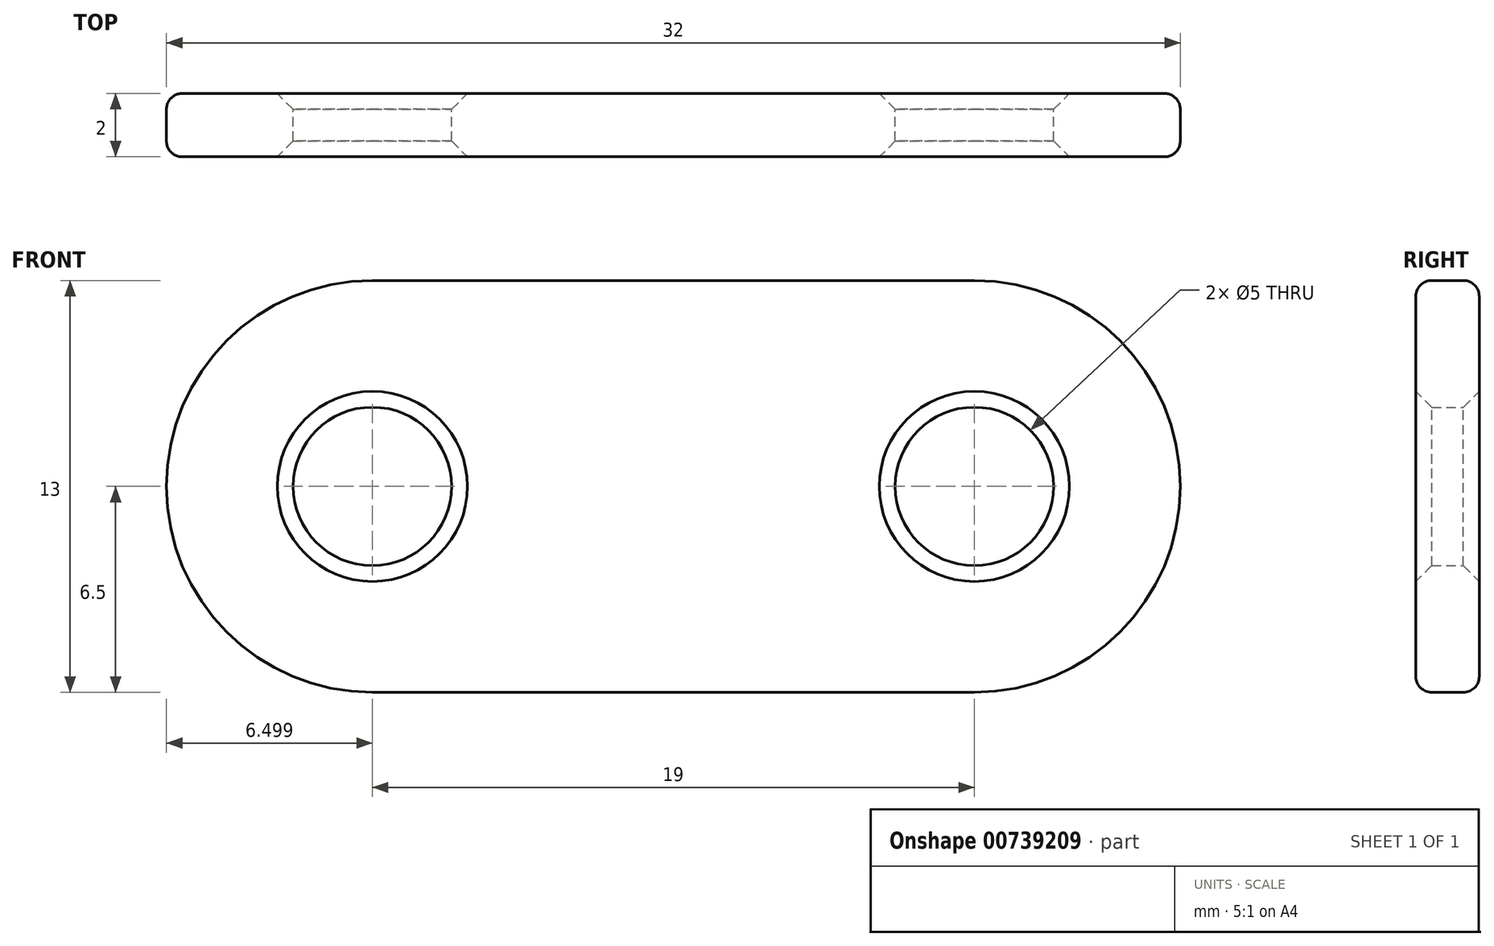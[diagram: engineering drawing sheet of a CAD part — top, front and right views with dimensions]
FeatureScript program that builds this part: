
annotation { "Feature Type Name" : "Feature", "Feature Type Description" : "" }
export const myFeature = defineFeature(function(context is Context, id is Id, definition is map)
    precondition{}
    {
        {
            var Q0;
            Q0=qCreatedBy(makeId("Front.planeOp"),FACE);
            var sketch = newSketch(context, id + "F0", { "sketchPlane" : qUnion([Q0])});
            skLineSegment(sketch, "E0", {"start": v(-21.64, 12.32) * mm, "end": v(-2.64, 12.32) * mm});
            skLineSegment(sketch, "E1", {"start": v(-21.64, -0.68) * mm, "end": v(-2.64, -0.68) * mm});
            skArc(sketch, "E2", {"start": v(-21.64, 12.32) * mm, "mid": v(-28.14, 5.82) * mm, "end": v(-21.64, -0.68) * mm});
            skArc(sketch, "E3", {"start": v(-2.64, -0.68) * mm, "mid": v(3.86, 5.82) * mm, "end": v(-2.64, 12.32) * mm});
            skCircle(sketch, "E4", {"center": v(-21.64, 5.82) * mm, "radius": 2.5 * mm});
            skCircle(sketch, "E5", {"center": v(-2.64, 5.82) * mm, "radius": 2.5 * mm});
            skSolve(sketch);
        }
        {
            var Q0;
            Q0 = qSketchRegion(id + "F0", true);
            extrude(context, id + "F1", {"entities" : qUnion([Q0]), "depth" : 2 * mm, "offsetDistance" : 25.4 * mm});
        }
        {
            var Q0;
            Q0=makeQuery(id+"F1.opExtrude","CAP_EDGE",EDGE,{"disambiguationData":[OSD([sQuery(id+"F0.wireOp",EDGE,"E4")])],"isStart":false});
            var Q1;
            Q1=makeQuery(id+"F1.opExtrude","CAP_EDGE",EDGE,{"disambiguationData":[OSD([sQuery(id+"F0.wireOp",EDGE,"E5")])],"isStart":false});
            var Q2;
            Q2=makeQuery(id+"F1.opExtrude","CAP_EDGE",EDGE,{"disambiguationData":[OSD([sQuery(id+"F0.wireOp",EDGE,"E5")])],"isStart":true});
            var Q3;
            Q3=makeQuery(id+"F1.opExtrude","CAP_EDGE",EDGE,{"disambiguationData":[OSD([sQuery(id+"F0.wireOp",EDGE,"E4")])],"isStart":true});
            chamfer(context, id + "F2", {"entities" : qUnion([Q0, Q1, Q2, Q3]), "width" : 0.5 * mm, "tangentPropagation" : true});
        }
        {
            var Q0;
            Q0=makeQuery(id+"F1.opExtrude","CAP_EDGE",EDGE,{"disambiguationData":[OSD([sQuery(id+"F0.wireOp",EDGE,"E0")])],"isStart":true});
            var Q1;
            Q1=makeQuery(id+"F1.opExtrude","CAP_EDGE",EDGE,{"disambiguationData":[OSD([sQuery(id+"F0.wireOp",EDGE,"E0")])],"isStart":false});
            fillet(context, id + "F3", {"entities" : qUnion([Q0, Q1]), "radius" : 0.5 * mm, "tangentPropagation" : true, "allowEdgeOverflow" : false});
        }
    });
